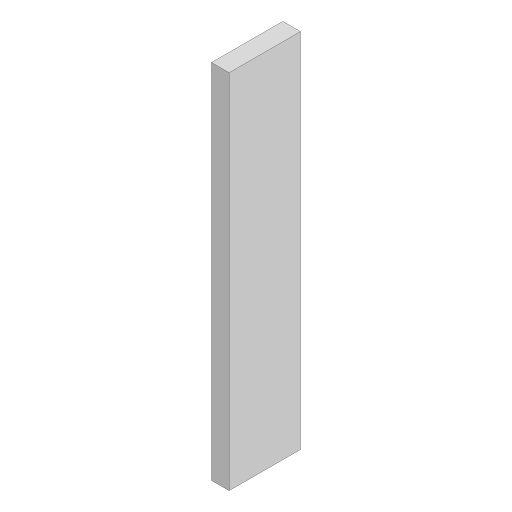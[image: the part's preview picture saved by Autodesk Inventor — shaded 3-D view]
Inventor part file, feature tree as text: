
AUTODESK INVENTOR PART (.ipt)
format: ipt  version: 2024 (Build 280153000, 153)  size: 82,944 bytes
history: native  units: in
note: dims shown in document units (in); Inventor stores cm internally (conversion verified against a paired STEP export)
features: extrude x1, sketch x1
ambient origin geometry x8: Origin, YZ Plane, XZ Plane, XY Plane, X Axis, Y Axis, Z Axis, Center Point
bodies: Solid1 (feature_tree)
feature tree (2):
  extrude  "Extrusion1"  Depth=10.315in
  sketch  "Sketch1"  dims[d0=2.5591in d1=10.315in d2=52.3425in d3=0.0in]
